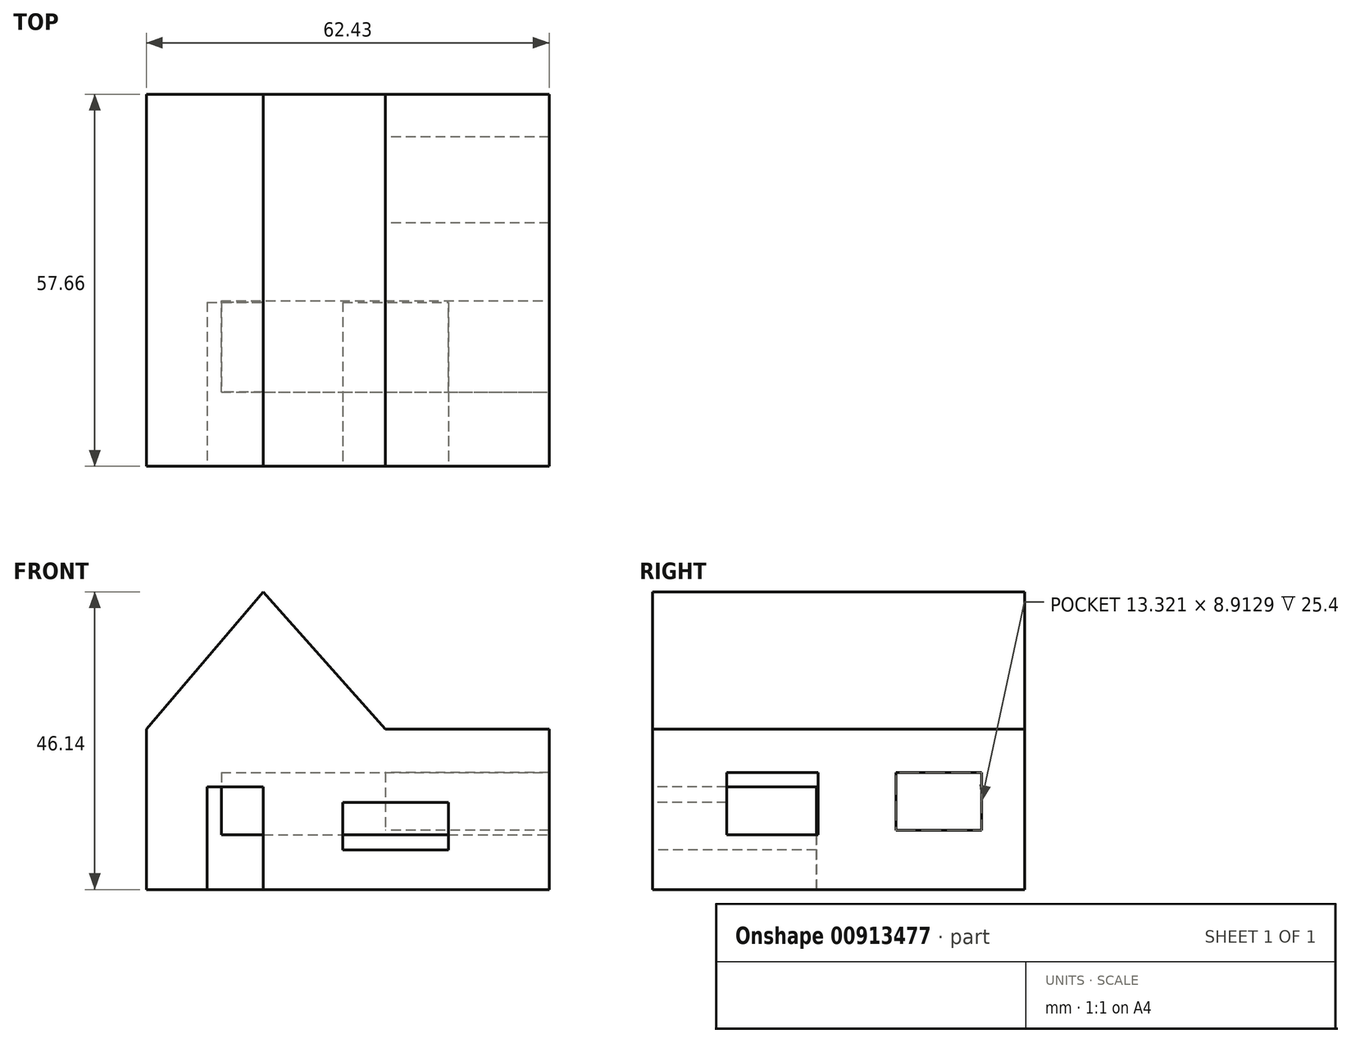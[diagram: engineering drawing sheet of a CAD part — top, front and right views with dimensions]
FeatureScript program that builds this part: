
annotation { "Feature Type Name" : "Feature", "Feature Type Description" : "" }
export const myFeature = defineFeature(function(context is Context, id is Id, definition is map)
    precondition{}
    {
        {
            var Q0;
            Q0=qCreatedBy(makeId("Front.planeOp"),FACE);
            var sketch = newSketch(context, id + "F0", { "sketchPlane" : qUnion([Q0])});
            skLineSegment(sketch, "E0", {"start": v(-18.14, -24.84) * mm, "end": v(-18.14, 0) * mm});
            skLineSegment(sketch, "E1", {"start": v(-18.14, -24.84) * mm, "end": v(18.89, -24.84) * mm});
            skLineSegment(sketch, "E2", {"start": v(18.89, -24.84) * mm, "end": v(18.89, 0) * mm});
            skLineSegment(sketch, "E3", {"start": v(-18.14, 0) * mm, "end": v(0, 21.3) * mm});
            skLineSegment(sketch, "E4", {"start": v(18.89, 0) * mm, "end": v(0, 21.3) * mm});
            skSolve(sketch);
        }
        {
            var Q0;
            Q0=makeQuery(id+"F0.imprint","IMPRINT",FACE,{"disambiguationData":[TD([[makeQuery(id+"F0.imprint","IMPRINT",EDGE,{"derivedFrom":sQuery(id+"F0.wireOp",EDGE,"E0")}),-1.0]])]});
            extrude(context, id + "F1", {"entities" : qUnion([Q0]), "depth" : 57.66 * mm, "offsetDistance" : 25.4 * mm});
        }
        {
            var Q0;
            Q0=makeQuery(id+"F1.opExtrude","CAP_FACE",FACE,{"disambiguationData":[OSD([sQuery(id+"F0.wireOp",EDGE,"E0"),sQuery(id+"F0.wireOp",EDGE,"E1"),sQuery(id+"F0.wireOp",EDGE,"E2"),sQuery(id+"F0.wireOp",EDGE,"E3"),sQuery(id+"F0.wireOp",EDGE,"E4")])],"isStart":false});
            var sketch = newSketch(context, id + "F2", { "sketchPlane" : qUnion([Q0])});
            skLineSegment(sketch, "E5", {"start": v(-8.73, -24.84) * mm, "end": v(-8.73, -8.95) * mm});
            skLineSegment(sketch, "E6", {"start": v(-8.73, -8.95) * mm, "end": v(0, -8.95) * mm});
            skLineSegment(sketch, "E7", {"start": v(0, -8.95) * mm, "end": v(0, -24.84) * mm});
            skSolve(sketch);
        }
        {
            var Q0;
            {var subQ0=sQuery(id+"F2.wireOp",EDGE,"E5");Q0=makeQuery(id+"F2.imprint","IMPRINT",FACE,{"disambiguationData":[TD([[makeQuery(id+"F2.imprint","IMPRINT",EDGE,{"derivedFrom":subQ0}),-1.0]])]});}
            extrude(context, id + "F3", {"entities" : qUnion([Q0]), "operationType" : NewBodyOperationType.REMOVE, "oppositeDirection" : true, "depth" : 25.4 * mm, "offsetDistance" : 25.4 * mm});
        }
        {
            var Q0;
            Q0=makeQuery(id+"F1.opExtrude","SWEPT_FACE",FACE,{"disambiguationData":[OSD([sQuery(id+"F0.wireOp",EDGE,"E2")])]});
            var sketch = newSketch(context, id + "F4", { "sketchPlane" : qUnion([Q0])});
            skLineSegment(sketch, "E8", {"start": v(-46.17, -6.73) * mm, "end": v(-46.17, -16.35) * mm});
            skLineSegment(sketch, "E9", {"start": v(-46.17, -6.73) * mm, "end": v(-32, -6.73) * mm});
            skLineSegment(sketch, "E10", {"start": v(-32, -6.73) * mm, "end": v(-32, -16.35) * mm});
            skLineSegment(sketch, "E11", {"start": v(-32, -16.35) * mm, "end": v(-46.17, -16.35) * mm});
            skLineSegment(sketch, "E12", {"start": v(-18.24, -6.73) * mm, "end": v(-18.24, -16.35) * mm});
            skLineSegment(sketch, "E13", {"start": v(-18.24, -16.35) * mm, "end": v(-3.63, -16.35) * mm});
            skLineSegment(sketch, "E14", {"start": v(-18.24, -6.73) * mm, "end": v(-3.63, -6.73) * mm});
            skLineSegment(sketch, "E15", {"start": v(-3.63, -6.73) * mm, "end": v(-3.63, -16.35) * mm});
            skSolve(sketch);
        }
        {
            var Q0;
            Q0=makeQuery(id+"F4.imprint","IMPRINT",FACE,{"disambiguationData":[TD([[makeQuery(id+"F4.imprint","IMPRINT",EDGE,{"derivedFrom":sQuery(id+"F4.wireOp",EDGE,"E8")}),1.0]])]});
            extrude(context, id + "F5", {"entities" : qUnion([Q0]), "operationType" : NewBodyOperationType.REMOVE, "oppositeDirection" : true, "depth" : 25.4 * mm, "offsetDistance" : 25.4 * mm});
        }
        {
            var Q0;
            Q0=makeQuery(id+"F1.opExtrude","SWEPT_FACE",FACE,{"disambiguationData":[OSD([sQuery(id+"F0.wireOp",EDGE,"E2")])]});
            var sketch = newSketch(context, id + "F6", { "sketchPlane" : qUnion([Q0])});
            skLineSegment(sketch, "E16", {"start": v(-19.96, -6.73) * mm, "end": v(-19.96, -15.64) * mm});
            skLineSegment(sketch, "E17", {"start": v(-19.96, -15.64) * mm, "end": v(-6.64, -15.64) * mm});
            skLineSegment(sketch, "E18", {"start": v(-6.64, -15.64) * mm, "end": v(-6.64, -6.73) * mm});
            skLineSegment(sketch, "E19", {"start": v(-6.64, -6.73) * mm, "end": v(-19.96, -6.73) * mm});
            skSolve(sketch);
        }
        {
            var Q0;
            Q0=makeQuery(id+"F6.imprint","IMPRINT",FACE,{"disambiguationData":[TD([[makeQuery(id+"F6.imprint","IMPRINT",EDGE,{"derivedFrom":sQuery(id+"F6.wireOp",EDGE,"E16")}),-1.0]])]});
            extrude(context, id + "F7", {"entities" : qUnion([Q0]), "operationType" : NewBodyOperationType.ADD, "depth" : 25.4 * mm, "offsetDistance" : 25.4 * mm});
        }
        {
            var Q0;
            {var subQ0=sQuery(id+"F0.wireOp",EDGE,"E2");Q0=makeQuery(id+"F7.boolean.opBoolean","MERGE",FACE,{"derivedFrom":[makeQuery(id+"F1.opExtrude","CAP_FACE",FACE,{"disambiguationData":[OSD([sQuery(id+"F0.wireOp",EDGE,"E0"),sQuery(id+"F0.wireOp",EDGE,"E1"),subQ0,sQuery(id+"F0.wireOp",EDGE,"E3"),sQuery(id+"F0.wireOp",EDGE,"E4")])],"isStart":false}),makeQuery(id+"F7.opExtrude","SWEPT_FACE",FACE,{"disambiguationData":[OSD([subQ0]),TDD([makeQuery(id+"F6.imprint","IMPRINT",EDGE,{"derivedFrom":makeQuery(id+"F1.opExtrude","CAP_EDGE",EDGE,{"disambiguationData":[OSD([subQ0])],"isStart":false})})])]})]});}
            var sketch = newSketch(context, id + "F8", { "sketchPlane" : qUnion([Q0])});
            skLineSegment(sketch, "E20", {"start": v(12.32, -11.34) * mm, "end": v(12.32, -18.73) * mm});
            skLineSegment(sketch, "E21", {"start": v(12.32, -11.34) * mm, "end": v(28.65, -11.34) * mm});
            skLineSegment(sketch, "E22", {"start": v(12.32, -18.73) * mm, "end": v(28.65, -18.73) * mm});
            skLineSegment(sketch, "E23", {"start": v(28.65, -18.73) * mm, "end": v(28.65, -11.34) * mm});
            skSolve(sketch);
        }
        {
            var Q0;
            Q0=makeQuery(id+"F8.imprint","IMPRINT",FACE,{"disambiguationData":[TD([[makeQuery(id+"F8.imprint","IMPRINT",EDGE,{"derivedFrom":sQuery(id+"F8.wireOp",EDGE,"E20")}),1.0]])]});
            extrude(context, id + "F9", {"entities" : qUnion([Q0]), "operationType" : NewBodyOperationType.REMOVE, "oppositeDirection" : true, "depth" : 25.4 * mm, "offsetDistance" : 25.4 * mm});
        }
    });
